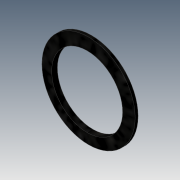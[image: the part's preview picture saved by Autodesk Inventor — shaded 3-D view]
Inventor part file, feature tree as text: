
AUTODESK INVENTOR PART (.ipt)
format: ipt  version: 2018.1 (Build 221171000, 171)  size: 94,208 bytes
history: native  units: mm
features: revolve x1, sketch x1
ambient origin geometry x8: Origin, YZ Plane, XZ Plane, XY Plane, X Axis, Y Axis, Z Axis, Center Point
bodies: Body1 (feature_tree)
feature tree (2):
  revolve  "Umdrehung1"
  sketch  "Skizze2"  dims[d5=2.443461mm d6=35.0mm d7=46.0mm d8=90.0deg]
